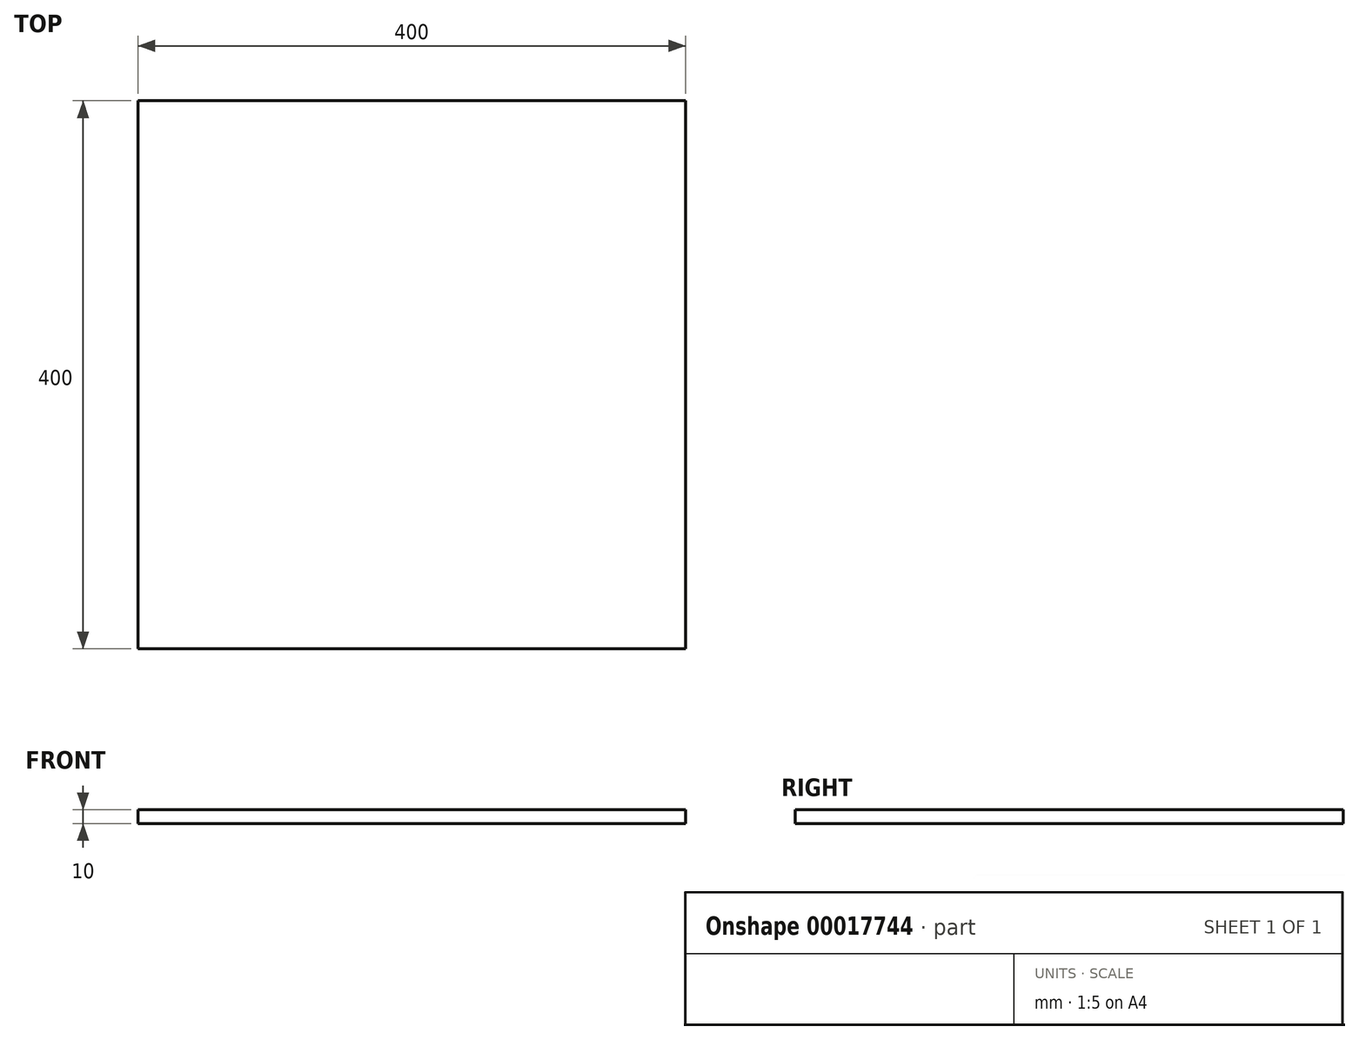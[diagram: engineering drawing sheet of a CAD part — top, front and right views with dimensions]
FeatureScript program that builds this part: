
annotation { "Feature Type Name" : "Feature", "Feature Type Description" : "" }
export const myFeature = defineFeature(function(context is Context, id is Id, definition is map)
    precondition{}
    {
        {
            var Q0;
            Q0=qCreatedBy(makeId("Top.planeOp"),FACE);
            var sketch = newSketch(context, id + "F0", { "sketchPlane" : qUnion([Q0])});
            skLineSegment(sketch, "E0.bottom", {"start": v(-70.96, 65.05) * mm, "end": v(329.04, 65.05) * mm});
            skLineSegment(sketch, "E0.top", {"start": v(-70.96, -334.95) * mm, "end": v(329.04, -334.95) * mm});
            skLineSegment(sketch, "E0.left", {"start": v(-70.96, 65.05) * mm, "end": v(-70.96, -334.95) * mm});
            skLineSegment(sketch, "E0.right", {"start": v(329.04, 65.05) * mm, "end": v(329.04, -334.95) * mm});
            skSolve(sketch);
        }
        {
            var Q0;
            Q0=qSketchRegion(id+"F0",true);
            extrude(context, id + "F1", {"entities" : qUnion([Q0]), "depth" : 10 * mm});
        }
    });
